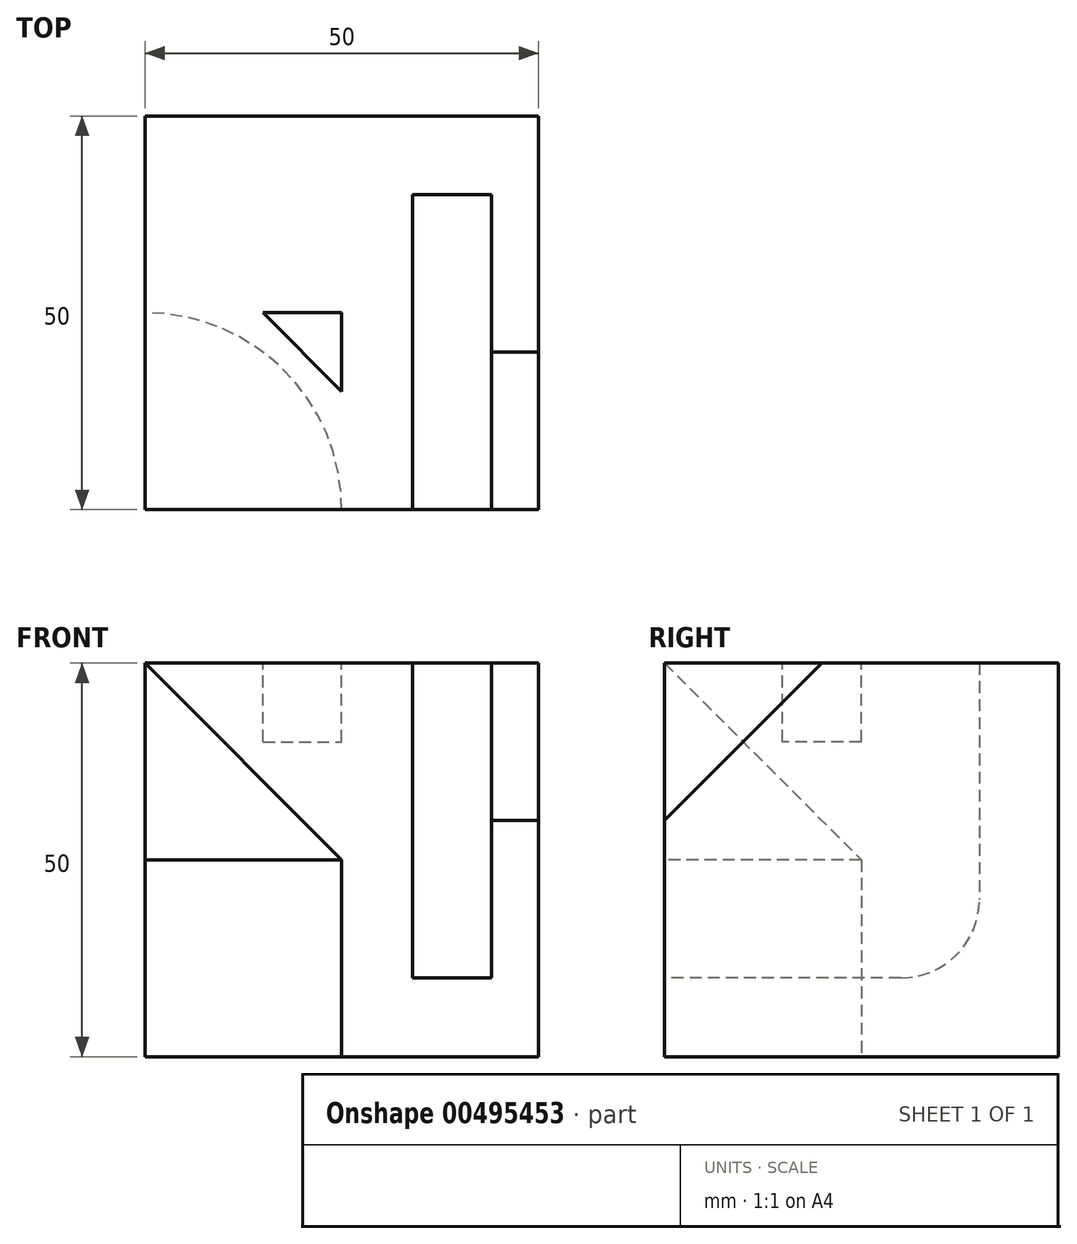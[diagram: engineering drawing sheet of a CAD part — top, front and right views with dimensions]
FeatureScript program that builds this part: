
annotation { "Feature Type Name" : "Feature", "Feature Type Description" : "" }
export const myFeature = defineFeature(function(context is Context, id is Id, definition is map)
    precondition{}
    {
        {
            var Q0;
            Q0=qCreatedBy(makeId("Front.planeOp"),FACE);
            var sketch = newSketch(context, id + "F0", { "sketchPlane" : qUnion([Q0])});
            skLineSegment(sketch, "E0.bottom", {"start": v(0, 0) * mm, "end": v(50, 0) * mm});
            skLineSegment(sketch, "E0.top", {"start": v(0, 50) * mm, "end": v(50, 50) * mm});
            skLineSegment(sketch, "E0.left", {"start": v(0, 0) * mm, "end": v(0, 50) * mm});
            skLineSegment(sketch, "E0.right", {"start": v(50, 0) * mm, "end": v(50, 50) * mm});
            skSolve(sketch);
        }
        {
            var Q0;
            Q0=makeQuery(id+"F0.imprint","IMPRINT",FACE,{"disambiguationData":[TD([[makeQuery(id+"F0.imprint","IMPRINT",EDGE,{"derivedFrom":sQuery(id+"F0.wireOp",EDGE,"E0.bottom")}),1.0]])]});
            extrude(context, id + "F1", {"entities" : qUnion([Q0]), "depth" : 50 * mm, "offsetDistance" : 25 * mm});
        }
        {
            var Q0;
            Q0=makeQuery(id+"F1.opExtrude","SWEPT_FACE",FACE,{"disambiguationData":[OSD([sQuery(id+"F0.wireOp",EDGE,"E0.right")])]});
            var sketch = newSketch(context, id + "F2", { "sketchPlane" : qUnion([Q0])});
            skLineSegment(sketch, "E1", {"start": v(-50, 50) * mm, "end": v(-50, 30) * mm});
            skLineSegment(sketch, "E2", {"start": v(-50, 30) * mm, "end": v(-30, 50) * mm});
            skLineSegment(sketch, "E3", {"start": v(-30, 50) * mm, "end": v(-50, 50) * mm});
            skSolve(sketch);
        }
        {
            var Q0;
            Q0=makeQuery(id+"F2.imprint","IMPRINT",FACE,{"disambiguationData":[TD([[makeQuery(id+"F2.imprint","IMPRINT",EDGE,{"derivedFrom":sQuery(id+"F2.wireOp",EDGE,"E1")}),-1.0]])]});
            extrude(context, id + "F3", {"entities" : qUnion([Q0]), "operationType" : NewBodyOperationType.REMOVE, "oppositeDirection" : true, "depth" : 6 * mm, "offsetDistance" : 25 * mm});
        }
        {
            var Q0;
            Q0=makeQuery(id+"F1.opExtrude","CAP_FACE",FACE,{"disambiguationData":[OSD([sQuery(id+"F0.wireOp",EDGE,"E0.bottom"),sQuery(id+"F0.wireOp",EDGE,"E0.top"),sQuery(id+"F0.wireOp",EDGE,"E0.left"),sQuery(id+"F0.wireOp",EDGE,"E0.right")])],"isStart":false});
            var sketch = newSketch(context, id + "F4", { "sketchPlane" : qUnion([Q0])});
            skLineSegment(sketch, "E4.bottom", {"start": v(44, 50) * mm, "end": v(34, 50) * mm});
            skLineSegment(sketch, "E4.top", {"start": v(44, 10) * mm, "end": v(34, 10) * mm});
            skLineSegment(sketch, "E4.left", {"start": v(44, 50) * mm, "end": v(44, 10) * mm});
            skLineSegment(sketch, "E4.right", {"start": v(34, 50) * mm, "end": v(34, 10) * mm});
            skSolve(sketch);
        }
        {
            var Q0;
            {var subQ3=sQuery(id+"F4.wireOp",EDGE,"E4.bottom");Q0=makeQuery(id+"F4.imprint","IMPRINT",FACE,{"disambiguationData":[TD([[makeQuery(id+"F4.imprint","IMPRINT",EDGE,{"derivedFrom":subQ3}),-1.0]])]});}
            extrude(context, id + "F5", {"entities" : qUnion([Q0]), "operationType" : NewBodyOperationType.REMOVE, "oppositeDirection" : true, "depth" : 40 * mm, "offsetDistance" : 25 * mm});
        }
        {
            var Q0;
            Q0=makeQuery(id+"F5.boolean.opBoolean","COPY",EDGE,{"derivedFrom":makeQuery(id+"F5.opExtrude","CAP_EDGE",EDGE,{"disambiguationData":[OSD([sQuery(id+"F4.wireOp",EDGE,"E4.top")])],"isStart":false})});
            fillet(context, id + "F6", {"entities" : qUnion([Q0]), "radius" : 10 * mm, "tangentPropagation" : true, "allowEdgeOverflow" : false});
        }
        {
            var Q0;
            Q0=makeQuery(id+"F1.opExtrude","SWEPT_FACE",FACE,{"disambiguationData":[OSD([sQuery(id+"F0.wireOp",EDGE,"E0.top")])]});
            var sketch = newSketch(context, id + "F7", { "sketchPlane" : qUnion([Q0])});
            skCircle(sketch, "E5", {"center": v(0, -50) * mm, "radius": 15 * mm});
            skLineSegment(sketch, "E6.bottom", {"start": v(0, -50) * mm, "end": v(25, -50) * mm});
            skLineSegment(sketch, "E6.top", {"start": v(0, -25) * mm, "end": v(25, -25) * mm});
            skLineSegment(sketch, "E6.left", {"start": v(0, -50) * mm, "end": v(0, -25) * mm});
            skLineSegment(sketch, "E6.right", {"start": v(25, -50) * mm, "end": v(25, -25) * mm});
            skLineSegment(sketch, "E7", {"start": v(25, -25) * mm, "end": v(15, -25) * mm});
            skLineSegment(sketch, "E8", {"start": v(15, -25) * mm, "end": v(25, -35) * mm});
            skLineSegment(sketch, "E9", {"start": v(25, -35) * mm, "end": v(25, -25) * mm});
            skSolve(sketch);
        }
        {
            var Q0;
            {var subQ1=sQuery(id+"F7.wireOp",EDGE,"E6.top");Q0=makeQuery(id+"F7.imprint","IMPRINT",FACE,{"disambiguationData":[TD([[makeQuery(id+"F7.imprint","IMPRINT",EDGE,{"derivedFrom":subQ1}),-1.0]])]});}
            extrude(context, id + "F8", {"entities" : qUnion([Q0]), "operationType" : NewBodyOperationType.REMOVE, "oppositeDirection" : true, "depth" : 10 * mm, "offsetDistance" : 25 * mm});
        }
        {
            var Q0;
            Q0=makeQuery(id+"F1.opExtrude","SWEPT_FACE",FACE,{"disambiguationData":[OSD([sQuery(id+"F0.wireOp",EDGE,"E0.bottom")])]});
            var sketch = newSketch(context, id + "F9", { "sketchPlane" : qUnion([Q0])});
            skCircle(sketch, "E10", {"center": v(0, 50) * mm, "radius": 25 * mm});
            skSolve(sketch);
        }
        {
            var Q0;
            {var subQ0=sQuery(id+"F9.wireOp",EDGE,"E10");var subQ1=sQuery(id+"F0.wireOp",EDGE,"E0.bottom");var subQ4=makeQuery(id+"F1.opExtrude","CAP_EDGE",EDGE,{"disambiguationData":[OSD([subQ1])],"isStart":false});var subQ5=makeQuery(id+"F9.imprint","INTERSECT",VERTEX,{"derivedFrom":[subQ4,subQ0]});Q0=makeQuery(id+"F9.imprint","IMPRINT",FACE,{"disambiguationData":[TD([[makeQuery(id+"F9.imprint","IMPRINT",EDGE,{"disambiguationData":[TD([[subQ5,1.0]])],"derivedFrom":subQ0}),1.0]])]});}
            extrude(context, id + "F10", {"entities" : qUnion([Q0]), "operationType" : NewBodyOperationType.REMOVE, "oppositeDirection" : true, "depth" : 25 * mm, "offsetDistance" : 25 * mm});
        }
        {
            var Q0;
            Q0=makeQuery(id+"F10.boolean.opBoolean","COPY",FACE,{"derivedFrom":makeQuery(id+"F10.opExtrude","CAP_FACE",FACE,{"disambiguationData":[OSD([sQuery(id+"F0.wireOp",EDGE,"E0.bottom"),sQuery(id+"F0.wireOp",EDGE,"E0.left"),sQuery(id+"F9.wireOp",EDGE,"E10")])],"isStart":false})});
            var sketch = newSketch(context, id + "F11", { "sketchPlane" : qUnion([Q0])});
            skCircle(sketch, "E11", {"center": v(0, 50) * mm, "radius": 25 * mm});
            skSolve(sketch);
        }
        {
            var Q0;
            Q0=makeQuery(id+"F1.opExtrude","CAP_FACE",FACE,{"disambiguationData":[OSD([sQuery(id+"F0.wireOp",EDGE,"E0.bottom"),sQuery(id+"F0.wireOp",EDGE,"E0.top"),sQuery(id+"F0.wireOp",EDGE,"E0.left"),sQuery(id+"F0.wireOp",EDGE,"E0.right")])],"isStart":false});
            var sketch = newSketch(context, id + "F12", { "sketchPlane" : qUnion([Q0])});
            skLineSegment(sketch, "E12", {"start": v(0, 50) * mm, "end": v(25, 25) * mm});
            skSolve(sketch);
        }
        {
            var Q0;
            Q0=makeQuery(id+"F1.opExtrude","SWEPT_FACE",FACE,{"disambiguationData":[OSD([sQuery(id+"F0.wireOp",EDGE,"E0.left")])]});
            var sketch = newSketch(context, id + "F13", { "sketchPlane" : qUnion([Q0])});
            skLineSegment(sketch, "E13", {"start": v(50, 50) * mm, "end": v(25, 25) * mm});
            skSolve(sketch);
        }
        {
            var Q0;
            Q0=makeQuery(id+"F12.imprint","IMPRINT",FACE,{"disambiguationData":[TD([[makeQuery(id+"F12.imprint","IMPRINT",EDGE,{"derivedFrom":sQuery(id+"F12.wireOp",EDGE,"E12")}),-1.0]])]});
            var Q1;
            Q1=makeQuery(id+"F13.imprint","IMPRINT",FACE,{"disambiguationData":[TD([[makeQuery(id+"F13.imprint","IMPRINT",EDGE,{"derivedFrom":sQuery(id+"F13.wireOp",EDGE,"E13")}),1.0]])]});
            var Q2;
            Q2=sQuery(id+"F11.wireOp",EDGE,"E11");
            revolve(context, id + "F14", {"operationType" : NewBodyOperationType.REMOVE, "entities" : qUnion([Q0, Q1]), "axis" : qUnion([Q2]), "revolveType" : RevolveType.FULL, "oppositeDirection" : true});
        }
    });
